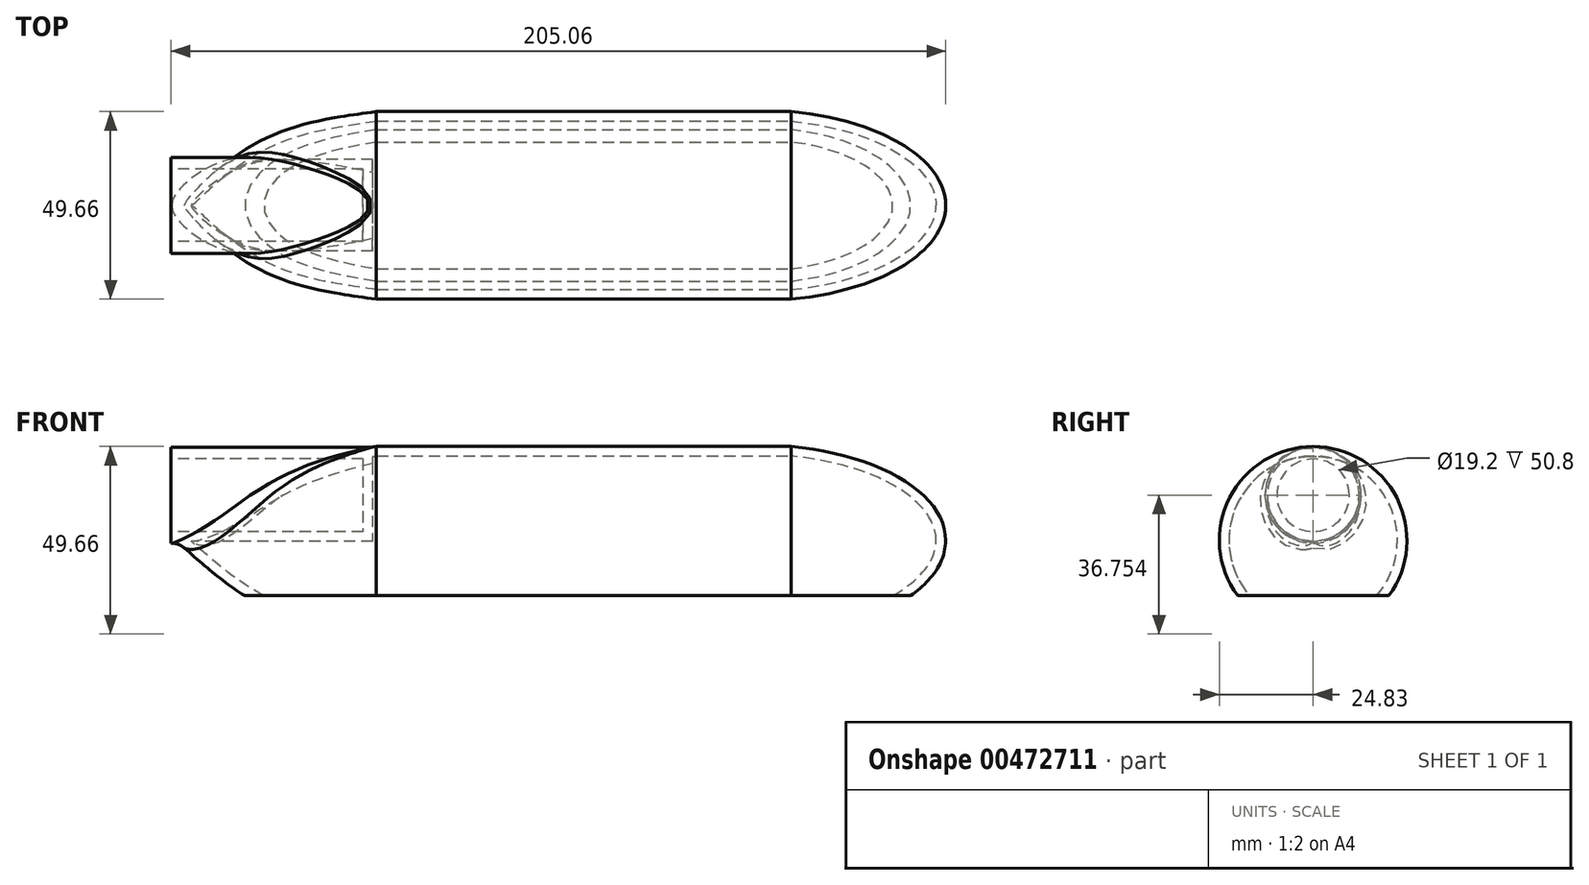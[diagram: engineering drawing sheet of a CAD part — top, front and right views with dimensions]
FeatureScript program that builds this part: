
annotation { "Feature Type Name" : "Feature", "Feature Type Description" : "" }
export const myFeature = defineFeature(function(context is Context, id is Id, definition is map)
    precondition{}
    {
        {
            var Q0;
            Q0=qCreatedBy(makeId("Front.planeOp"),FACE);
            var sketch = newSketch(context, id + "F0", { "sketchPlane" : qUnion([Q0])});
            skLineSegment(sketch, "E0", {"start": v(-31.61, 11.92) * mm, "end": v(-133.22, 11.92) * mm, "construction": true});
            skLineSegment(sketch, "E1.0", {"start": v(-34.79, 21.45) * mm, "end": v(-85.59, 21.45) * mm});
            skLineSegment(sketch, "E2.0", {"start": v(-31.61, 24.62) * mm, "end": v(-85.59, 24.62) * mm});
            skLineSegment(sketch, "E3", {"start": v(-31.61, 24.62) * mm, "end": v(-31.61, 11.92) * mm});
            skLineSegment(sketch, "E4.0", {"start": v(-34.79, 21.45) * mm, "end": v(-34.79, 11.92) * mm});
            skLineSegment(sketch, "E5.0", {"start": v(-85.59, 24.62) * mm, "end": v(-85.59, 21.45) * mm});
            skLineSegment(sketch, "E6", {"start": v(-34.79, 11.92) * mm, "end": v(-31.61, 11.92) * mm});
            skSolve(sketch);
        }
        {
            var Q0;
            Q0=makeQuery(id+"F0.imprint","IMPRINT",FACE,{"disambiguationData":[TD([[makeQuery(id+"F0.imprint","IMPRINT",EDGE,{"derivedFrom":sQuery(id+"F0.wireOp",EDGE,"E1.0")}),-1.0]])]});
            var Q1;
            Q1=sQuery(id+"F0.wireOp",EDGE,"E0");
            revolve(context, id + "F1", {"entities" : qUnion([Q0]), "axis" : qUnion([Q1]), "revolveType" : RevolveType.FULL});
        }
        {
            var Q0;
            Q0=qCreatedBy(makeId("Front.planeOp"),FACE);
            var sketch = newSketch(context, id + "F2", { "sketchPlane" : qUnion([Q0])});
            skLineSegment(sketch, "E7", {"start": v(-31.33, 24.83) * mm, "end": v(85.63, 24.83) * mm});
            skLineSegment(sketch, "E8", {"start": v(119.47, 0) * mm, "end": v(-84.35, 0) * mm});
            skEllipticalArc(sketch, "E9.trimOffspring", {});
            skPoint(sketch, "E10.1.internal.orphan", {"position": v(-58.03, 24.83) * mm});
            skFitSpline(sketch, "E11", {"points": [v(-31.33, 24.83) * mm, v(-59.9, 18.06) * mm, v(-84.35, 0) * mm], "startDerivative": vector(-59.93, -8.16) * mm, "endDerivative": vector(-46.16, -41.4) * mm});
            const initialGuessF2  = {"E9.trimOffspring": [0.06983201205730438, 0, 1, 0, 0.04963874816894531, 0.02521649581516408, 0, 1.7463622005121493]};
            skSetInitialGuess(sketch, initialGuessF2);
            skSolve(sketch);
        }
        {
            var Q0;
            {var subQ1=sQuery(id+"F2.wireOp",EDGE,"E8");Q0=makeQuery(id+"F2.imprint","IMPRINT",FACE,{"disambiguationData":[TD([[makeQuery(id+"F2.imprint","IMPRINT",EDGE,{"derivedFrom":subQ1}),-1.0]])]});}
            var Q1;
            Q1=sQuery(id+"F2.wireOp",EDGE,"E8");
            revolve(context, id + "F3", {"operationType" : NewBodyOperationType.ADD, "entities" : qUnion([Q0]), "axis" : qUnion([Q1]), "revolveType" : RevolveType.FULL});
        }
        {
            var Q0;
            Q0=qCreatedBy(makeId("Front.planeOp"),FACE);
            cPlane(context, id + "F4", {"entities" : qUnion([Q0]), "cplaneType" : CPlaneType.OFFSET, "offset" : 25.4 * mm, "width" : 152.4 * mm, "height" : 152.4 * mm});
        }
        {
            var Q0;
            Q0=qCreatedBy(id+"F4.planeOp",FACE);
            var sketch = newSketch(context, id + "F5", { "sketchPlane" : qUnion([Q0])});
            skLineSegment(sketch, "E12.bottom", {"start": v(-76.83, -14.66) * mm, "end": v(136.4, -14.66) * mm});
            skLineSegment(sketch, "E12.top", {"start": v(-76.83, -37.6) * mm, "end": v(136.4, -37.6) * mm});
            skLineSegment(sketch, "E12.left", {"start": v(-76.83, -14.66) * mm, "end": v(-76.83, -37.6) * mm});
            skLineSegment(sketch, "E12.right", {"start": v(136.4, -14.66) * mm, "end": v(136.4, -37.6) * mm});
            skSolve(sketch);
        }
        {
            var Q0;
            Q0 = qSketchRegion(id + "F5", true);
            extrude(context, id + "F6", {"entities" : qUnion([Q0]), "operationType" : NewBodyOperationType.REMOVE, "oppositeDirection" : true, "depth" : 76.2 * mm});
        }
        {
            var Q0;
            Q0=makeQuery(id+"F1.opRevolve","SWEPT_FACE",FACE,{"disambiguationData":[OSD([sQuery(id+"F0.wireOp",EDGE,"E5.0")])]});
            var sketch = newSketch(context, id + "F7", { "sketchPlane" : qUnion([Q0])});
            skCircle(sketch, "E13", {"center": v(0, 11.92) * mm, "radius": 9.6 * mm});
            skSolve(sketch);
        }
        {
            var Q0;
            Q0 = qSketchRegion(id + "F7", true);
            extrude(context, id + "F8", {"entities" : qUnion([Q0]), "operationType" : NewBodyOperationType.REMOVE, "oppositeDirection" : true, "depth" : 50.8 * mm});
        }
        {
            var Q0;
            Q0=makeQuery(id+"F3.boolean.opBoolean","INTERSECT",EDGE,{"derivedFrom":[makeQuery(id+"F1.opRevolve","SWEPT_FACE",FACE,{"disambiguationData":[OSD([sQuery(id+"F0.wireOp",EDGE,"E2.0")])]}),makeQuery(id+"F3.opRevolve","SWEPT_FACE",FACE,{"disambiguationData":[OSD([sQuery(id+"F2.wireOp",EDGE,"E11")])]})]});
            fillet(context, id + "F9", {"entities" : qUnion([Q0]), "radius" : 5.08 * mm, "tangentPropagation" : true, "allowEdgeOverflow" : false});
        }
        {
            var Q0;
            Q0=makeQuery(id+"F6.boolean.opBoolean","COPY",FACE,{"derivedFrom":makeQuery(id+"F6.opExtrude","SWEPT_FACE",FACE,{"disambiguationData":[OSD([sQuery(id+"F5.wireOp",EDGE,"E12.bottom")])]})});
            shell(context, id + "F10", {"entities" : qUnion([Q0]), "thickness" : 2.54 * mm});
        }
    });
